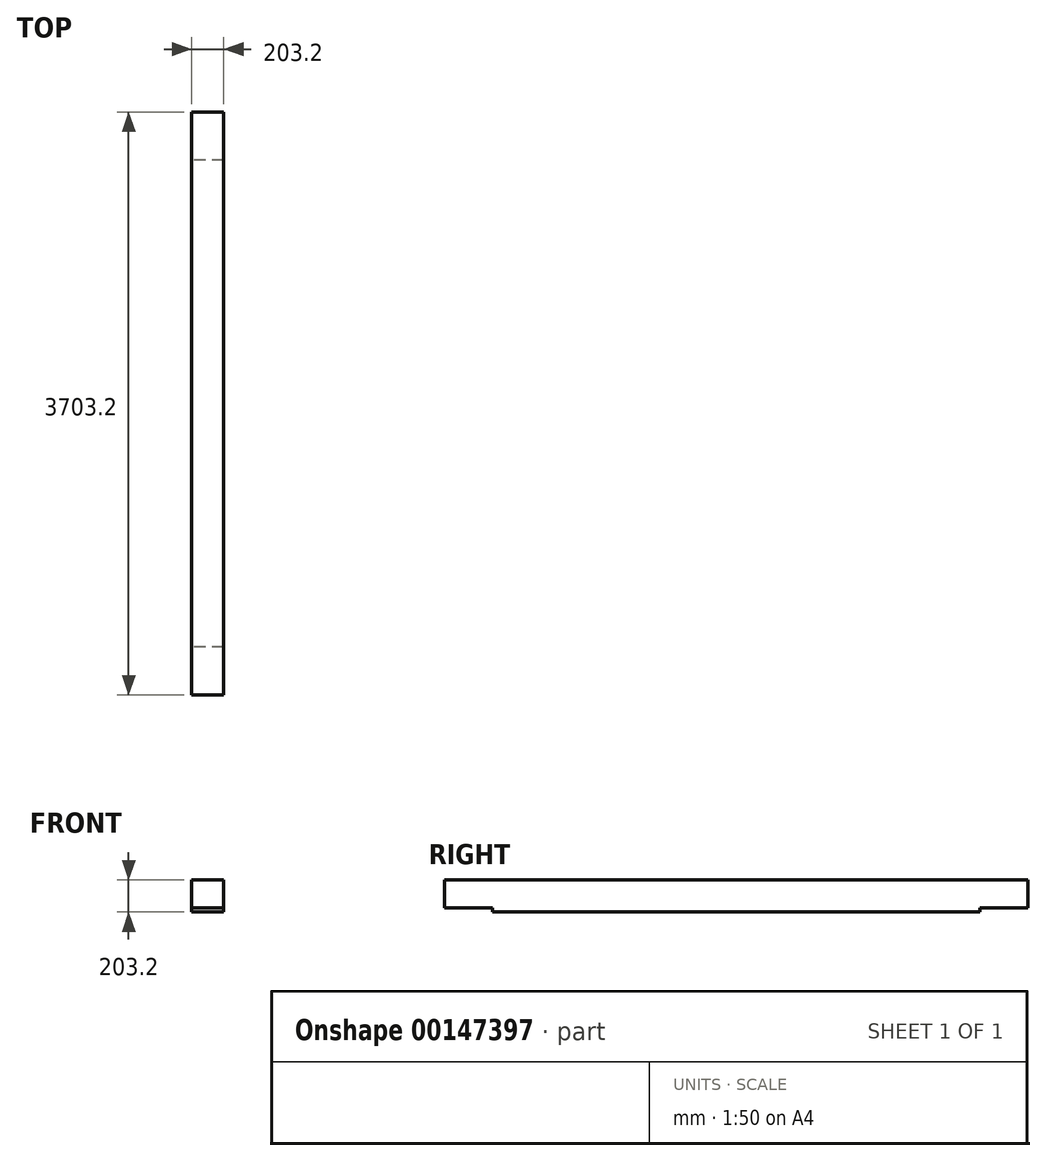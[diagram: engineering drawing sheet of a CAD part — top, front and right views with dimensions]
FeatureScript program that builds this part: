
annotation { "Feature Type Name" : "Feature", "Feature Type Description" : "" }
export const myFeature = defineFeature(function(context is Context, id is Id, definition is map)
    precondition{}
    {
        {
            var Q0;
            Q0=qCreatedBy(makeId("Right.planeOp"),FACE);
            var sketch = newSketch(context, id + "F0", { "sketchPlane" : qUnion([Q0])});
            skLineSegment(sketch, "E0.bottom", {"start": v(-1546.8, 0) * mm, "end": v(1546.8, 0) * mm});
            skLineSegment(sketch, "E0.top", {"start": v(-1851.6, 203.2) * mm, "end": v(1851.6, 203.2) * mm});
            skLineSegment(sketch, "E0.left", {"start": v(-1851.6, 25.4) * mm, "end": v(-1851.6, 203.2) * mm});
            skLineSegment(sketch, "E0.right", {"start": v(1851.6, 25.4) * mm, "end": v(1851.6, 203.2) * mm});
            skLineSegment(sketch, "E1.top", {"start": v(-1851.6, 25.4) * mm, "end": v(-1546.8, 25.4) * mm});
            skLineSegment(sketch, "E2.MirrorCS", {"start": v(1851.6, 25.4) * mm, "end": v(1546.8, 25.4) * mm});
            skLineSegment(sketch, "E3", {"start": v(-1546.8, 0) * mm, "end": v(-1546.8, 25.4) * mm});
            skPoint(sketch, "E1.right.end.orphan", {"position": v(-1443.6, 25.4) * mm});
            skLineSegment(sketch, "E4", {"start": v(1546.8, 0) * mm, "end": v(1546.8, 25.4) * mm});
            skPoint(sketch, "E4.endSnap0", {"position": v(1647.6, 25.4) * mm});
            skPoint(sketch, "E5.MirrorCS.end.orphan", {"position": v(1443.6, 25.4) * mm});
            skSolve(sketch);
        }
        {
            var Q0;
            Q0 = qSketchRegion(id + "F0", true);
            extrude(context, id + "F1", {"entities" : qUnion([Q0]), "depth" : 203.2 * mm});
        }
    });
